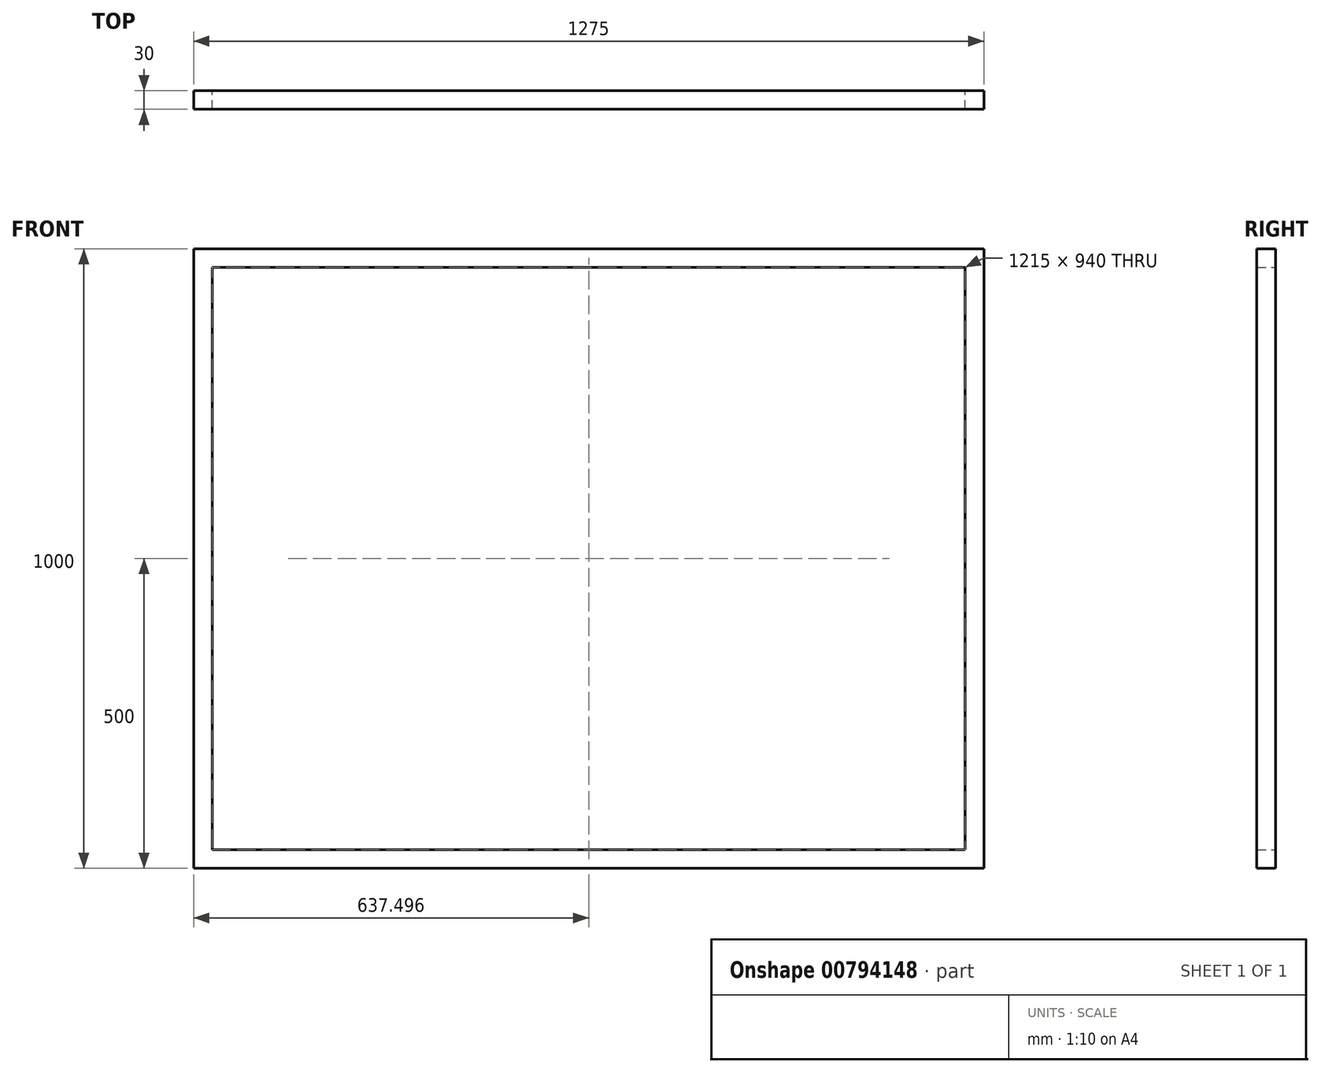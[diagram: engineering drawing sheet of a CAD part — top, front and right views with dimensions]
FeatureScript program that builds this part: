
annotation { "Feature Type Name" : "Feature", "Feature Type Description" : "" }
export const myFeature = defineFeature(function(context is Context, id is Id, definition is map)
    precondition{}
    {
        {
            var Q0;
            Q0=qCreatedBy(makeId("Front.planeOp"),FACE);
            var sketch = newSketch(context, id + "F0", { "sketchPlane" : qUnion([Q0])});
            skLineSegment(sketch, "E0.bottom", {"start": v(-49.46, 0) * mm, "end": v(1225.54, 0) * mm});
            skLineSegment(sketch, "E0.top", {"start": v(-49.46, 1000) * mm, "end": v(1225.54, 1000) * mm});
            skLineSegment(sketch, "E0.left", {"start": v(-49.46, 0) * mm, "end": v(-49.46, 1000) * mm});
            skLineSegment(sketch, "E0.right", {"start": v(1225.54, 0) * mm, "end": v(1225.54, 1000) * mm});
            skLineSegment(sketch, "E1.0", {"start": v(-19.46, 970) * mm, "end": v(1195.54, 970) * mm});
            skLineSegment(sketch, "E1.1", {"start": v(-19.46, 30) * mm, "end": v(-19.46, 970) * mm});
            skLineSegment(sketch, "E1.2", {"start": v(-19.46, 30) * mm, "end": v(1195.54, 30) * mm});
            skLineSegment(sketch, "E1.3", {"start": v(1195.54, 30) * mm, "end": v(1195.54, 970) * mm});
            skLineSegment(sketch, "E2", {"start": v(-19.46, 970) * mm, "end": v(588.04, 30) * mm});
            skLineSegment(sketch, "E3", {"start": v(588.04, 30) * mm, "end": v(623.76, 30) * mm});
            skLineSegment(sketch, "E4", {"start": v(623.76, 30) * mm, "end": v(16.26, 970) * mm});
            skLineSegment(sketch, "E5", {"start": v(16.26, 970) * mm, "end": v(-19.46, 970) * mm});
            skLineSegment(sketch, "E6", {"start": v(66.26, 970) * mm, "end": v(673.76, 30) * mm});
            skLineSegment(sketch, "E7", {"start": v(709.48, 30) * mm, "end": v(101.98, 970) * mm});
            skLineSegment(sketch, "E8", {"start": v(151.98, 970) * mm, "end": v(759.48, 30) * mm});
            skLineSegment(sketch, "E9", {"start": v(795.2, 30) * mm, "end": v(187.7, 970) * mm});
            skLineSegment(sketch, "E10", {"start": v(237.7, 970) * mm, "end": v(845.2, 30) * mm});
            skLineSegment(sketch, "E11", {"start": v(880.92, 30) * mm, "end": v(273.42, 970) * mm});
            skLineSegment(sketch, "E12", {"start": v(323.42, 970) * mm, "end": v(930.92, 30) * mm});
            skLineSegment(sketch, "E13", {"start": v(966.63, 30) * mm, "end": v(359.13, 970) * mm});
            skLineSegment(sketch, "E14", {"start": v(409.13, 970) * mm, "end": v(1016.63, 30) * mm});
            skLineSegment(sketch, "E15", {"start": v(1052.35, 30) * mm, "end": v(444.85, 970) * mm});
            skLineSegment(sketch, "E16", {"start": v(494.85, 970) * mm, "end": v(1102.35, 30) * mm});
            skLineSegment(sketch, "E17", {"start": v(1138.07, 30) * mm, "end": v(530.57, 970) * mm});
            skLineSegment(sketch, "E18", {"start": v(580.57, 970) * mm, "end": v(1188.07, 30) * mm});
            skLineSegment(sketch, "E19", {"start": v(1223.8, 30) * mm, "end": v(616.3, 970) * mm});
            skSolve(sketch);
        }
        {
            var Q0;
            Q0=makeQuery(id+"F0.imprint","IMPRINT",FACE,{"disambiguationData":[TD([[makeQuery(id+"F0.imprint","IMPRINT",EDGE,{"derivedFrom":sQuery(id+"F0.wireOp",EDGE,"E0.bottom")}),1.0]])]});
            extrude(context, id + "F1", {"entities" : qUnion([Q0]), "depth" : 30 * mm, "offsetDistance" : 25 * mm});
        }
    });
